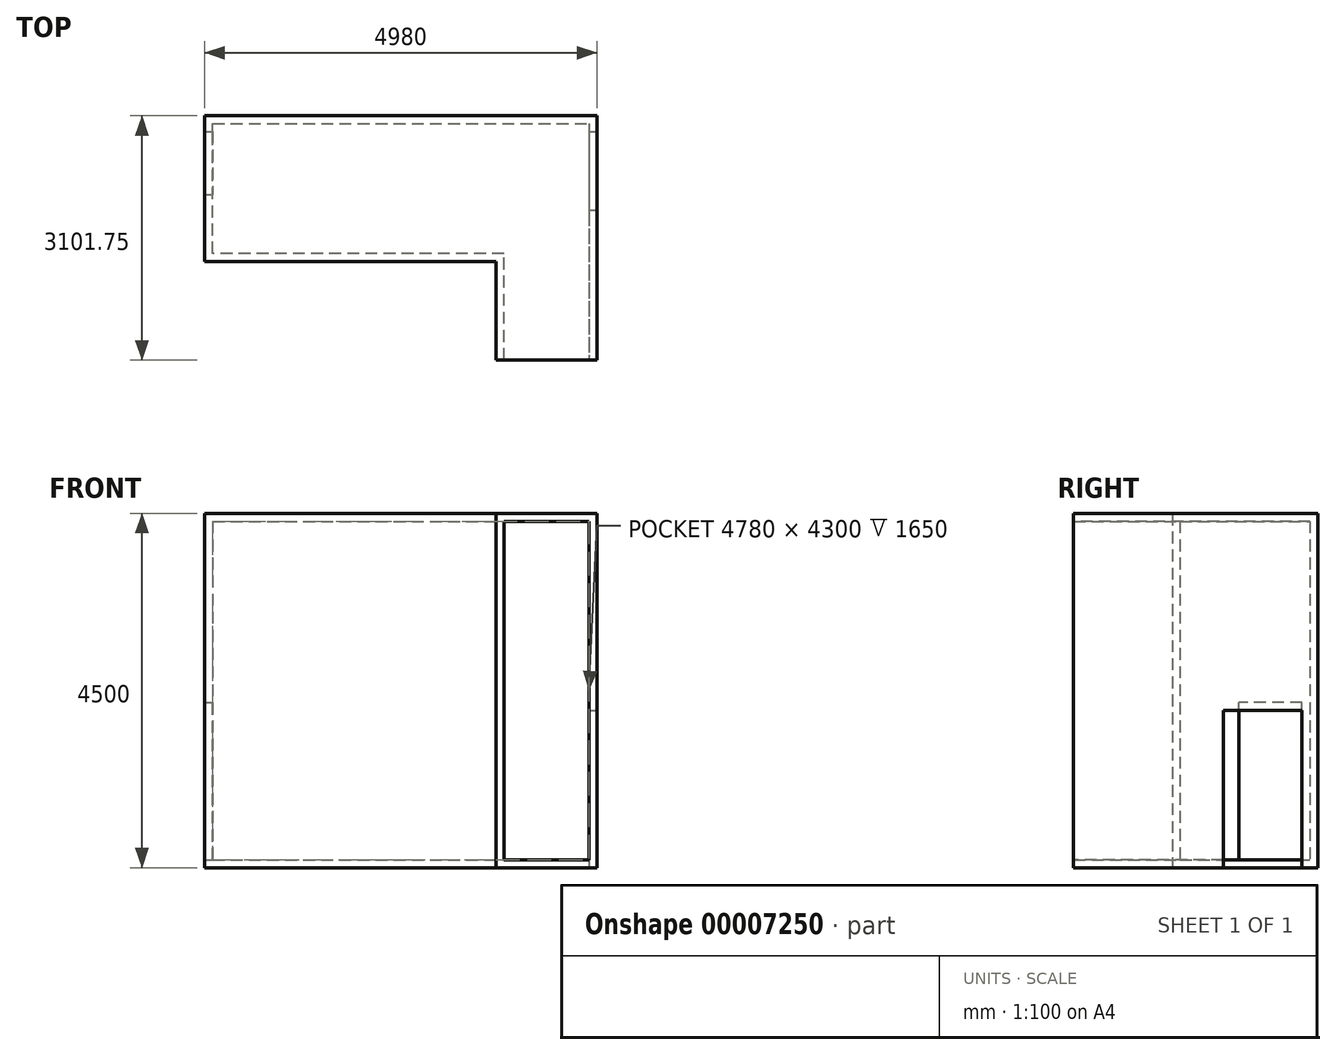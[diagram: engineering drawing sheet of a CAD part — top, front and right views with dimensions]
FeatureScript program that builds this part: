
annotation { "Feature Type Name" : "Feature", "Feature Type Description" : "" }
export const myFeature = defineFeature(function(context is Context, id is Id, definition is map)
    precondition{}
    {
        {
            var Q0;
            Q0=qCreatedBy(makeId("Top.planeOp"),FACE);
            var sketch = newSketch(context, id + "F0", { "sketchPlane" : qUnion([Q0])});
            skLineSegment(sketch, "E0.0", {"start": v(4880, 1750) * mm, "end": v(4880, -1351.75) * mm});
            skLineSegment(sketch, "E0.1", {"start": v(-100, 1750) * mm, "end": v(4880, 1750) * mm});
            skLineSegment(sketch, "E0.2", {"start": v(-100, -100) * mm, "end": v(-100, 1750) * mm});
            skLineSegment(sketch, "E0.3", {"start": v(3600, -100) * mm, "end": v(-100, -100) * mm});
            skLineSegment(sketch, "E0.4", {"start": v(3600, -1351.75) * mm, "end": v(3600, -100) * mm});
            skLineSegment(sketch, "E1", {"start": v(3600, -1351.75) * mm, "end": v(4880, -1351.75) * mm});
            skSolve(sketch);
        }
        {
            var Q0;
            Q0=makeQuery(id+"F0.imprint","IMPRINT",FACE,{"disambiguationData":[TD([[makeQuery(id+"F0.imprint","IMPRINT",EDGE,{"derivedFrom":sQuery(id+"F0.wireOp",EDGE,"E0.0")}),-1.0]])]});
            extrude(context, id + "F1", {"entities" : qUnion([Q0]), "depth" : 4500 * mm});
        }
        {
            var Q0;
            Q0=makeQuery(id+"F1.opExtrude","SWEPT_FACE",FACE,{"disambiguationData":[OSD([sQuery(id+"F0.wireOp",EDGE,"E1")])]});
            shell(context, id + "F2", {"entities" : qUnion([Q0]), "thickness" : 100 * mm});
        }
        {
            var Q0;
            Q0=makeQuery(id+"F1.opExtrude","SWEPT_FACE",FACE,{"disambiguationData":[OSD([sQuery(id+"F0.wireOp",EDGE,"E0.0")])]});
            var sketch = newSketch(context, id + "F3", { "sketchPlane" : qUnion([Q0])});
            skLineSegment(sketch, "E2", {"start": v(1550, 0) * mm, "end": v(1550, 2000) * mm});
            skLineSegment(sketch, "E3", {"start": v(1550, 2000) * mm, "end": v(550, 2000) * mm});
            skLineSegment(sketch, "E4", {"start": v(550, 2000) * mm, "end": v(550, 0) * mm});
            skSolve(sketch);
        }
        {
            var Q0;
            Q0 = qSketchRegion(id + "F3", true);
            var Q1;
            {var subQ2=sQuery(id+"F3.wireOp",EDGE,"E2");Q1=makeQuery(id+"F3.imprint","IMPRINT",FACE,{"disambiguationData":[TD([[makeQuery(id+"F3.imprint","IMPRINT",EDGE,{"derivedFrom":subQ2}),1.0]])]});}
            extrude(context, id + "F4", {"entities" : qUnion([Q0, Q1]), "operationType" : NewBodyOperationType.REMOVE, "oppositeDirection" : true, "depth" : 100 * mm});
        }
        {
            var Q0;
            Q0=makeQuery(id+"F2.opShell","OFFSET_FACE",FACE,{"disambiguationData":[OSD([sQuery(id+"F0.wireOp",EDGE,"E0.2")])]});
            var sketch = newSketch(context, id + "F5", { "sketchPlane" : qUnion([Q0])});
            skLineSegment(sketch, "E5.bottom", {"start": v(1550, 100) * mm, "end": v(750, 100) * mm});
            skLineSegment(sketch, "E5.top", {"start": v(1550, 2100) * mm, "end": v(750, 2100) * mm});
            skLineSegment(sketch, "E5.left", {"start": v(1550, 100) * mm, "end": v(1550, 2100) * mm});
            skLineSegment(sketch, "E5.right", {"start": v(750, 100) * mm, "end": v(750, 2100) * mm});
            skSolve(sketch);
        }
        {
            var Q0;
            Q0=makeQuery(id+"F5.imprint","IMPRINT",FACE,{"disambiguationData":[TD([[makeQuery(id+"F5.imprint","IMPRINT",EDGE,{"derivedFrom":sQuery(id+"F5.wireOp",EDGE,"E5.bottom")}),1.0]])]});
            extrude(context, id + "F6", {"entities" : qUnion([Q0]), "operationType" : NewBodyOperationType.REMOVE, "oppositeDirection" : true, "depth" : 100 * mm});
        }
    });
